# Revit family: American Oak Veneer Chevron
name_source: partatom
category: Generic Models
revit_build: Autodesk Revit 2017 (Build: 20170419_0315(x64)
units: mm (PartAtom-declared; Revit-internal decimal feet)

## family parameters
Always vertical = Yes
Can host rebar = No
Cut with Voids When Loaded = No
Part Type = Normal
Room Calculation Point = No
Round Connector Dimension = Use Diameter
Shared = Yes
Work Plane-Based = No

## types (1)
- 2400 x 1200
    Clear Finish Code = EX24 AO-CHE-CF
    Description = American Oak Veneer
    Manufacturer = Easycraft Australia Pty Ltd ph 07 3906 7200
    Material = <By Category>
    Model = Expression Series - Chevron
    Panel_height = 2400 mm  [stored 7.87402 ft]
    Panel_thickness = 10 mm  [stored 0.0328084 ft]
    Panel_width = 1200 mm  [stored 3.93701 ft]
    Raw Finish Code = EX24 AO-CHE
    URL = https://www.easycraft.com.au

note: [stored X ft] marks values corroborated as IEEE doubles in the binary element streams (Revit-internal decimal feet)

## geometry (parser evidence)
native form markers: Blend x2, Sweep x2
no freeform markers — native parametric forms only
